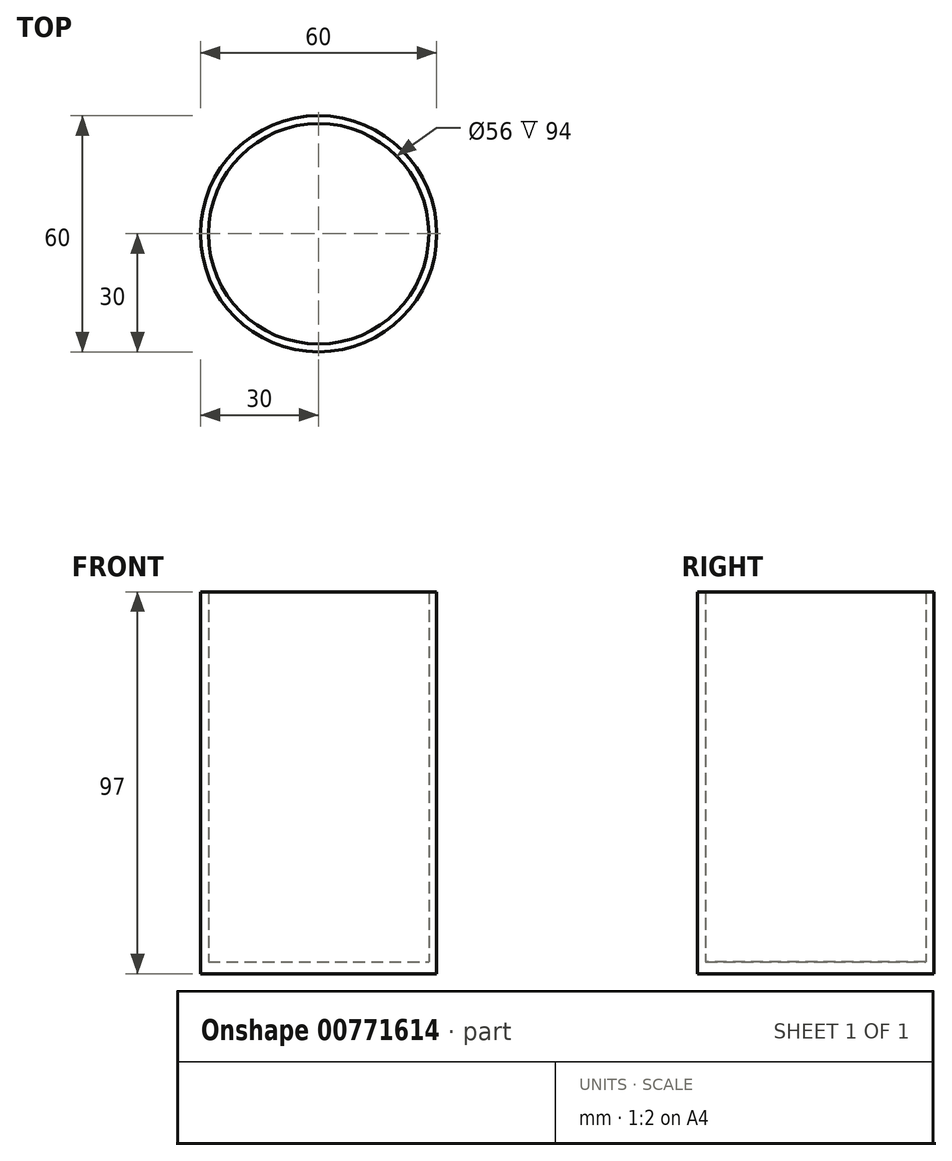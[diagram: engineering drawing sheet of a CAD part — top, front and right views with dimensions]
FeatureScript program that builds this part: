
annotation { "Feature Type Name" : "Feature", "Feature Type Description" : "" }
export const myFeature = defineFeature(function(context is Context, id is Id, definition is map)
    precondition{}
    {
        {
            var Q0;
            Q0=qCreatedBy(makeId("Front.planeOp"),FACE);
            var sketch = newSketch(context, id + "F0", { "sketchPlane" : qUnion([Q0])});
            skLineSegment(sketch, "E0", {"start": v(-30, 97) * mm, "end": v(-30, 0) * mm});
            skLineSegment(sketch, "E1", {"start": v(-30, 0) * mm, "end": v(0, 0) * mm});
            skLineSegment(sketch, "E2", {"start": v(0, 0) * mm, "end": v(0, 3) * mm});
            skLineSegment(sketch, "E3", {"start": v(0, 3) * mm, "end": v(-28, 3) * mm});
            skLineSegment(sketch, "E4", {"start": v(-28, 3) * mm, "end": v(-28, 97) * mm});
            skLineSegment(sketch, "E5", {"start": v(-28, 97) * mm, "end": v(-30, 97) * mm});
            skLineSegment(sketch, "E6", {"start": v(0, 0) * mm, "end": v(0, 124.36) * mm, "construction": true});
            skSolve(sketch);
        }
        {
            var Q0;
            Q0=makeQuery(id+"F0.imprint","IMPRINT",FACE,{"disambiguationData":[TD([[makeQuery(id+"F0.imprint","IMPRINT",EDGE,{"derivedFrom":sQuery(id+"F0.wireOp",EDGE,"E0")}),1.0]])]});
            var Q1;
            Q1=sQuery(id+"F0.wireOp",EDGE,"E6");
            revolve(context, id + "F1", {"surfaceOperationType" : NewSurfaceOperationType.NEW, "entities" : qUnion([Q0]), "axis" : qUnion([Q1]), "revolveType" : RevolveType.FULL});
        }
    });
